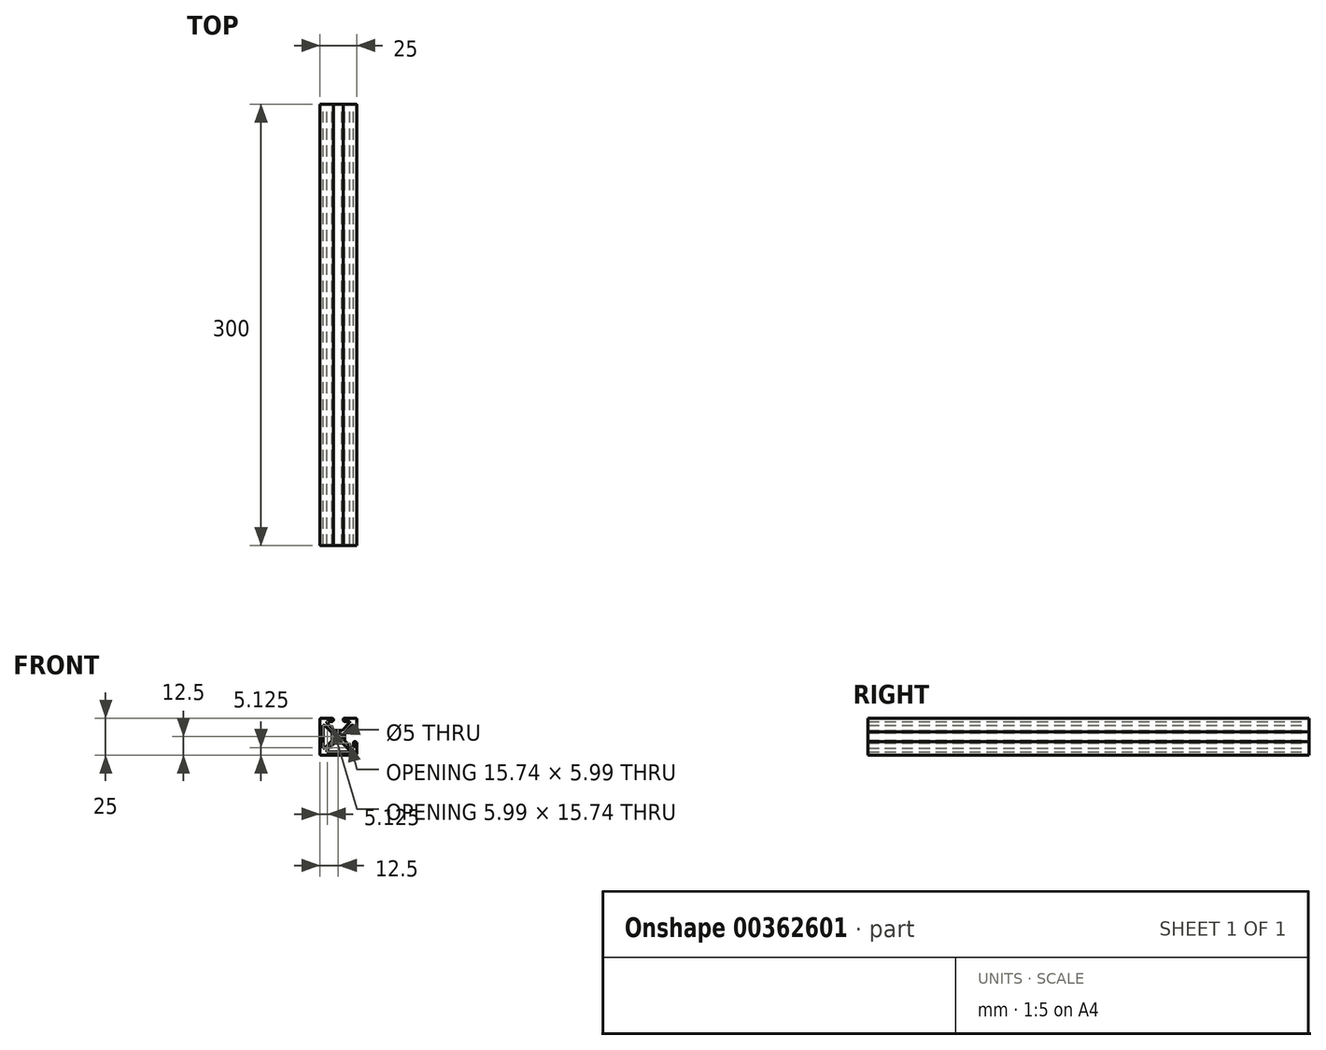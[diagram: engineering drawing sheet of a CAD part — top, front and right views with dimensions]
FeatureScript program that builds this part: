
annotation { "Feature Type Name" : "Feature", "Feature Type Description" : "" }
export const myFeature = defineFeature(function(context is Context, id is Id, definition is map)
    precondition{}
    {
        {
            var Q0;
            Q0=qCreatedBy(makeId("Front.planeOp"),FACE);
            var sketch = newSketch(context, id + "F0", { "sketchPlane" : qUnion([Q0])});
            skCircle(sketch, "E0", {"center": v(0, 0) * mm, "radius": 2.5 * mm});
            skLineSegment(sketch, "E1.bottom", {"start": v(11.8, 12.5) * mm, "end": v(4.31, 12.5) * mm});
            skLineSegment(sketch, "E1.top", {"start": v(11.8, -12.5) * mm, "end": v(-11.8, -12.5) * mm});
            skLineSegment(sketch, "E1.left", {"start": v(12.5, 11.8) * mm, "end": v(12.5, 4.31) * mm});
            skLineSegment(sketch, "E1.right", {"start": v(-12.5, 11.8) * mm, "end": v(-12.5, -11.8) * mm});
            skLineSegment(sketch, "E2.bottom", {"start": v(2.58, 4.38) * mm, "end": v(-2.58, 4.38) * mm});
            skLineSegment(sketch, "E2.top", {"start": v(2.58, -4.38) * mm, "end": v(-2.58, -4.38) * mm});
            skLineSegment(sketch, "E2.left", {"start": v(4.38, 2.58) * mm, "end": v(4.38, -2.58) * mm});
            skLineSegment(sketch, "E2.right", {"start": v(-4.38, 2.58) * mm, "end": v(-4.38, -2.58) * mm});
            skLineSegment(sketch, "E3.bottom", {"start": v(-7.17, 10.37) * mm, "end": v(-4.31, 10.37) * mm});
            skLineSegment(sketch, "E3.top", {"start": v(-7.17, -10.37) * mm, "end": v(7.17, -10.37) * mm});
            skLineSegment(sketch, "E3.left", {"start": v(-10.37, 7.17) * mm, "end": v(-10.37, -7.17) * mm});
            skLineSegment(sketch, "E3.right", {"start": v(10.37, 7.17) * mm, "end": v(10.37, 4.31) * mm});
            skLineSegment(sketch, "E4.0", {"start": v(-3.25, 11.44) * mm, "end": v(-3.25, 11.44) * mm});
            skLineSegment(sketch, "E5.0", {"start": v(3.25, 11.44) * mm, "end": v(3.25, 11.44) * mm});
            skArc(sketch, "E6", {"start": v(-4.31, 10.37) * mm, "mid": v(-3.25, 11.43) * mm, "end": v(-4.31, 12.5) * mm});
            skPoint(sketch, "E6.first.point", {"position": v(-4.31, 12.5) * mm});
            skPoint(sketch, "E6.second.point", {"position": v(-3.25, 11.44) * mm});
            skPoint(sketch, "E6.third.point", {"position": v(-4.31, 10.37) * mm});
            skArc(sketch, "E7", {"start": v(4.31, 12.5) * mm, "mid": v(3.25, 11.44) * mm, "end": v(4.31, 10.37) * mm});
            skPoint(sketch, "E7.first.point", {"position": v(4.31, 10.37) * mm});
            skPoint(sketch, "E7.second.point", {"position": v(3.25, 11.44) * mm});
            skPoint(sketch, "E7.third.point", {"position": v(4.31, 12.5) * mm});
            skArc(sketch, "E8", {"start": v(10.37, 4.31) * mm, "mid": v(11.43, 3.25) * mm, "end": v(12.5, 4.31) * mm});
            skPoint(sketch, "E8.first.point", {"position": v(10.37, 4.31) * mm});
            skPoint(sketch, "E8.second.point", {"position": v(11.45, 3.25) * mm});
            skPoint(sketch, "E8.third.point", {"position": v(12.5, 4.31) * mm});
            skArc(sketch, "E9", {"start": v(12.5, -4.31) * mm, "mid": v(11.44, -3.25) * mm, "end": v(10.37, -4.31) * mm});
            skPoint(sketch, "E9.first.point", {"position": v(12.5, -4.31) * mm});
            skPoint(sketch, "E9.second.point", {"position": v(11.4, -3.25) * mm});
            skPoint(sketch, "E9.third.point", {"position": v(10.37, -4.31) * mm});
            skLineSegment(sketch, "E10.trimOffspring", {"start": v(-4.31, 12.5) * mm, "end": v(-11.8, 12.5) * mm});
            skLineSegment(sketch, "E11.trimOffspring", {"start": v(4.31, 10.37) * mm, "end": v(7.17, 10.37) * mm});
            skLineSegment(sketch, "E12.trimOffspring", {"start": v(12.5, -4.31) * mm, "end": v(12.5, -11.8) * mm});
            skLineSegment(sketch, "E13.trimOffspring", {"start": v(10.37, -4.31) * mm, "end": v(10.37, -7.17) * mm});
            skLineSegment(sketch, "E14.0", {"start": v(4.59, -3.08) * mm, "end": v(9.18, -7.67) * mm});
            skLineSegment(sketch, "E15.0", {"start": v(3.08, -4.59) * mm, "end": v(7.67, -9.18) * mm});
            skLineSegment(sketch, "E16.1.0", {"start": v(-3.08, -4.59) * mm, "end": v(-7.67, -9.18) * mm});
            skLineSegment(sketch, "E16.1.1", {"start": v(-4.59, -3.08) * mm, "end": v(-9.18, -7.67) * mm});
            skLineSegment(sketch, "E16.2.0", {"start": v(-4.59, 3.08) * mm, "end": v(-9.18, 7.67) * mm});
            skLineSegment(sketch, "E16.2.1", {"start": v(-3.08, 4.59) * mm, "end": v(-7.67, 9.18) * mm});
            skLineSegment(sketch, "E16.3.0", {"start": v(3.08, 4.59) * mm, "end": v(7.67, 9.18) * mm});
            skLineSegment(sketch, "E16.3.1", {"start": v(4.59, 3.08) * mm, "end": v(9.18, 7.67) * mm});
            skLineSegment(sketch, "E17", {"start": v(-10.37, 0) * mm, "end": v(20.35, 0) * mm});
            skPoint(sketch, "E17.endSnap0", {"position": v(4.38, 0) * mm});
            skPoint(sketch, "E18.newPointA", {"position": v(-10.37, 10.37) * mm});
            skArc(sketch, "E18.filletArc", {"start": v(-9.18, 7.67) * mm, "mid": v(-9.94, 7.82) * mm, "end": v(-10.37, 7.17) * mm});
            skArc(sketch, "E19.filletArc", {"start": v(10.37, 7.17) * mm, "mid": v(9.94, 7.82) * mm, "end": v(9.18, 7.67) * mm});
            skPoint(sketch, "E20.newPointB", {"position": v(10.37, 10.37) * mm});
            skArc(sketch, "E20.filletArc", {"start": v(7.67, 9.18) * mm, "mid": v(7.82, 9.94) * mm, "end": v(7.17, 10.37) * mm});
            skArc(sketch, "E21.filletArc", {"start": v(9.18, -7.67) * mm, "mid": v(9.94, -7.82) * mm, "end": v(10.37, -7.17) * mm});
            skPoint(sketch, "E22.newPointA", {"position": v(10.37, -10.37) * mm});
            skArc(sketch, "E22.filletArc", {"start": v(7.17, -10.37) * mm, "mid": v(7.82, -9.94) * mm, "end": v(7.67, -9.18) * mm});
            skPoint(sketch, "E23.newPointB", {"position": v(-10.37, -10.37) * mm});
            skArc(sketch, "E23.filletArc", {"start": v(-7.67, -9.18) * mm, "mid": v(-7.82, -9.94) * mm, "end": v(-7.17, -10.37) * mm});
            skArc(sketch, "E24.filletArc", {"start": v(-10.37, -7.17) * mm, "mid": v(-9.94, -7.82) * mm, "end": v(-9.18, -7.67) * mm});
            skArc(sketch, "E25.filletArc", {"start": v(-7.17, 10.37) * mm, "mid": v(-7.82, 9.94) * mm, "end": v(-7.67, 9.18) * mm});
            skPoint(sketch, "E26.newPointB", {"position": v(-4.38, 4.38) * mm});
            skArc(sketch, "E26.filletArc", {"start": v(-4.38, 2.58) * mm, "mid": v(-4.43, 2.85) * mm, "end": v(-4.59, 3.08) * mm});
            skPoint(sketch, "E27.newPointB", {"position": v(-4.38, -4.38) * mm});
            skArc(sketch, "E27.filletArc", {"start": v(-4.59, -3.08) * mm, "mid": v(-4.43, -2.85) * mm, "end": v(-4.38, -2.58) * mm});
            skArc(sketch, "E28.filletArc", {"start": v(-3.08, 4.59) * mm, "mid": v(-2.85, 4.43) * mm, "end": v(-2.58, 4.38) * mm});
            skPoint(sketch, "E29.newPointA", {"position": v(4.38, 4.38) * mm});
            skArc(sketch, "E29.filletArc", {"start": v(2.58, 4.38) * mm, "mid": v(2.85, 4.43) * mm, "end": v(3.08, 4.59) * mm});
            skArc(sketch, "E30.filletArc", {"start": v(4.59, 3.08) * mm, "mid": v(4.43, 2.85) * mm, "end": v(4.38, 2.58) * mm});
            skPoint(sketch, "E31.newPointA", {"position": v(4.38, -4.38) * mm});
            skArc(sketch, "E31.filletArc", {"start": v(4.38, -2.58) * mm, "mid": v(4.43, -2.85) * mm, "end": v(4.59, -3.08) * mm});
            skArc(sketch, "E32.filletArc", {"start": v(3.08, -4.59) * mm, "mid": v(2.85, -4.43) * mm, "end": v(2.58, -4.38) * mm});
            skArc(sketch, "E33.filletArc", {"start": v(-2.58, -4.38) * mm, "mid": v(-2.85, -4.43) * mm, "end": v(-3.08, -4.59) * mm});
            skPoint(sketch, "E34.visualSharp", {"position": v(12.5, 12.5) * mm});
            skArc(sketch, "E34.filletArc", {"start": v(12.5, 11.8) * mm, "mid": v(12.3, 12.3) * mm, "end": v(11.8, 12.5) * mm});
            skPoint(sketch, "E35.visualSharp", {"position": v(-12.5, 12.5) * mm});
            skArc(sketch, "E35.filletArc", {"start": v(-11.8, 12.5) * mm, "mid": v(-12.3, 12.3) * mm, "end": v(-12.5, 11.8) * mm});
            skPoint(sketch, "E36.visualSharp", {"position": v(-12.5, -12.5) * mm});
            skArc(sketch, "E36.filletArc", {"start": v(-12.5, -11.8) * mm, "mid": v(-12.3, -12.3) * mm, "end": v(-11.8, -12.5) * mm});
            skPoint(sketch, "E37.visualSharp", {"position": v(12.5, -12.5) * mm});
            skArc(sketch, "E37.filletArc", {"start": v(11.8, -12.5) * mm, "mid": v(12.3, -12.3) * mm, "end": v(12.5, -11.8) * mm});
            skSolve(sketch);
        }
        {
            var Q0;
            {var subQ13=sQuery(id+"F0.wireOp",EDGE,"E1.bottom");Q0=makeQuery(id+"F0.imprint","IMPRINT",FACE,{"disambiguationData":[TD([[makeQuery(id+"F0.imprint","IMPRINT",EDGE,{"derivedFrom":subQ13}),1.0]])]});}
            extrude(context, id + "F1", {"entities" : qUnion([Q0]), "depth" : 300 * mm});
        }
    });
